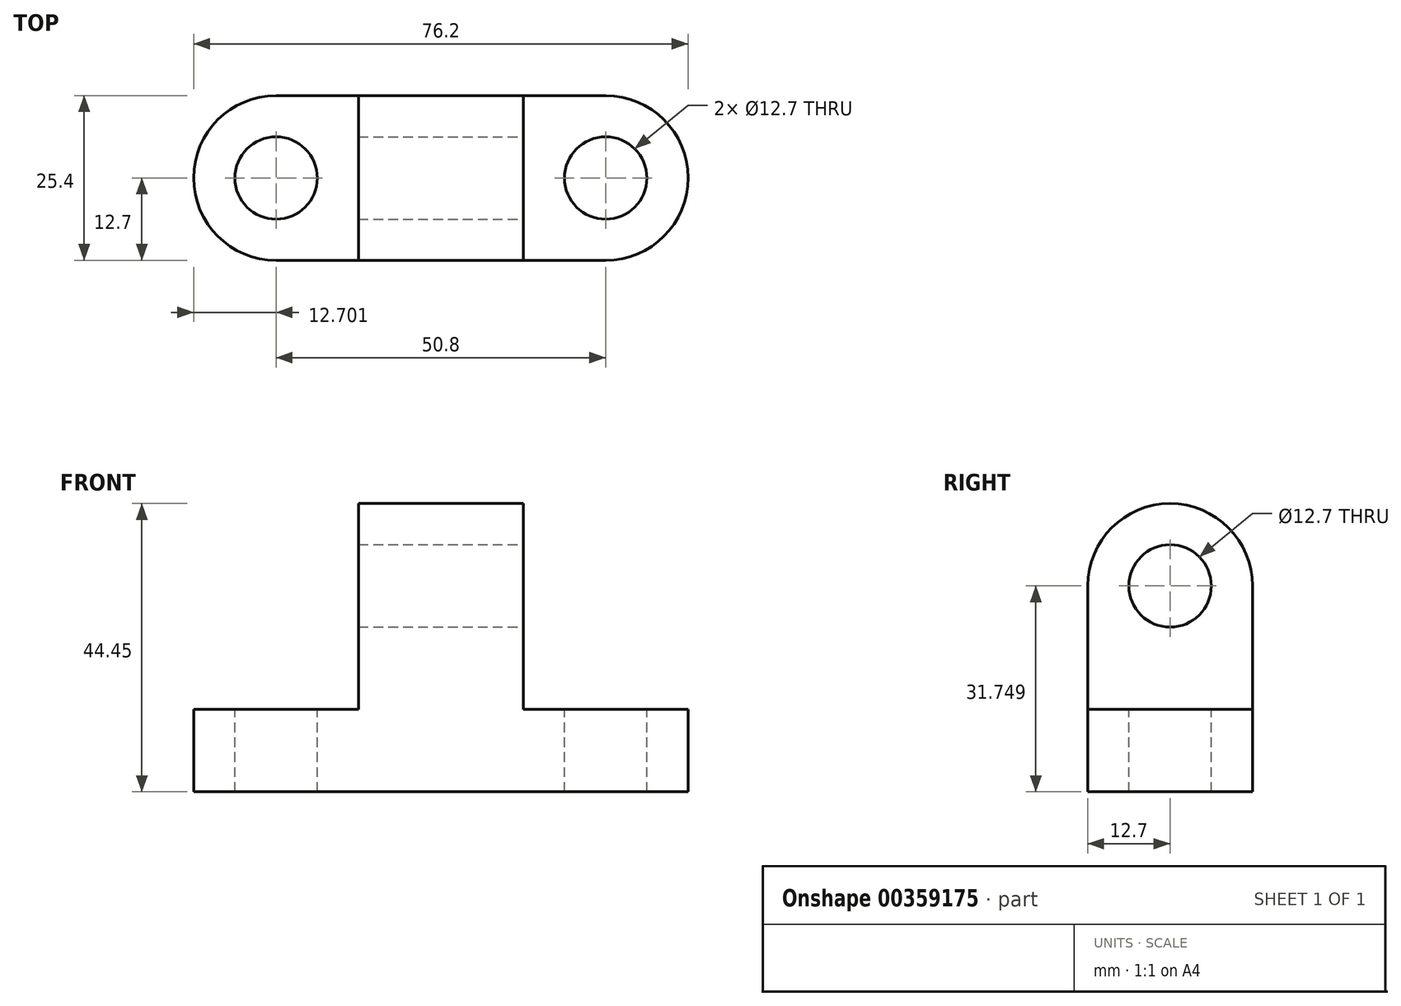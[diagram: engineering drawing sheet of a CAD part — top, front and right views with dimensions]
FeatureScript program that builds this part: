
annotation { "Feature Type Name" : "Feature", "Feature Type Description" : "" }
export const myFeature = defineFeature(function(context is Context, id is Id, definition is map)
    precondition{}
    {
        {
            var Q0;
            Q0=qCreatedBy(makeId("Front.planeOp"),FACE);
            var sketch = newSketch(context, id + "F0", { "sketchPlane" : qUnion([Q0])});
            skLineSegment(sketch, "E0", {"start": v(-54.44, 55.85) * mm, "end": v(-54.44, 24.1) * mm});
            skLineSegment(sketch, "E1", {"start": v(-54.44, 24.1) * mm, "end": v(-79.84, 24.1) * mm});
            skLineSegment(sketch, "E2", {"start": v(-79.84, 24.1) * mm, "end": v(-79.84, 11.4) * mm});
            skLineSegment(sketch, "E3", {"start": v(-79.84, 11.4) * mm, "end": v(-3.64, 11.4) * mm});
            skLineSegment(sketch, "E4", {"start": v(-3.64, 11.4) * mm, "end": v(-3.64, 24.1) * mm});
            skLineSegment(sketch, "E5", {"start": v(-3.64, 24.1) * mm, "end": v(-29.04, 24.1) * mm});
            skLineSegment(sketch, "E6", {"start": v(-29.04, 24.1) * mm, "end": v(-29.04, 55.85) * mm});
            skLineSegment(sketch, "E7", {"start": v(-29.04, 55.85) * mm, "end": v(-54.44, 55.85) * mm});
            skSolve(sketch);
        }
        {
            var Q0;
            Q0=makeQuery(id+"F0.imprint","IMPRINT",FACE,{"disambiguationData":[TD([[makeQuery(id+"F0.imprint","IMPRINT",EDGE,{"derivedFrom":sQuery(id+"F0.wireOp",EDGE,"E0")}),1.0]])]});
            extrude(context, id + "F1", {"entities" : qUnion([Q0]), "depth" : 25.4 * mm});
        }
        {
            var Q0;
            Q0=makeQuery(id+"F1.opExtrude","SWEPT_FACE",FACE,{"disambiguationData":[OSD([sQuery(id+"F0.wireOp",EDGE,"E6")])]});
            var sketch = newSketch(context, id + "F2", { "sketchPlane" : qUnion([Q0])});
            skLineSegment(sketch, "E8", {"start": v(-25.4, 24.1) * mm, "end": v(-25.4, 43.15) * mm});
            skLineSegment(sketch, "E9", {"start": v(-12.7, 55.85) * mm, "end": v(-12.7, 55.85) * mm});
            skLineSegment(sketch, "E10", {"start": v(0, 43.15) * mm, "end": v(0, 24.1) * mm});
            skPoint(sketch, "E11.visualSharp", {"position": v(-25.4, 55.85) * mm});
            skArc(sketch, "E11.filletArc", {"start": v(-12.7, 55.85) * mm, "mid": v(-21.68, 52.13) * mm, "end": v(-25.4, 43.15) * mm});
            skPoint(sketch, "E12.visualSharp", {"position": v(0, 55.85) * mm});
            skArc(sketch, "E12.filletArc", {"start": v(0, 43.15) * mm, "mid": v(-3.72, 52.13) * mm, "end": v(-12.7, 55.85) * mm});
            skCircle(sketch, "E13", {"center": v(-12.7, 43.15) * mm, "radius": 6.35 * mm});
            skSolve(sketch);
        }
        {
            var Q0;
            Q0=makeQuery(id+"F2.imprint","IMPRINT",FACE,{"disambiguationData":[TD([[makeQuery(id+"F2.imprint","IMPRINT",EDGE,{"derivedFrom":sQuery(id+"F2.wireOp",EDGE,"E13")}),1.0]])]});
            var Q1;
            {var subQ0=sQuery(id+"F2.wireOp",EDGE,"E11.filletArc");Q1=makeQuery(id+"F2.imprint","IMPRINT",FACE,{"disambiguationData":[TD([[makeQuery(id+"F2.imprint","IMPRINT",EDGE,{"derivedFrom":subQ0}),-1.0]])]});}
            var Q2;
            {var subQ0=sQuery(id+"F2.wireOp",EDGE,"E12.filletArc");Q2=makeQuery(id+"F2.imprint","IMPRINT",FACE,{"disambiguationData":[TD([[makeQuery(id+"F2.imprint","IMPRINT",EDGE,{"derivedFrom":subQ0}),-1.0]])]});}
            extrude(context, id + "F3", {"entities" : qUnion([Q0, Q1, Q2]), "operationType" : NewBodyOperationType.REMOVE, "oppositeDirection" : true, "depth" : 25.4 * mm});
        }
        {
            var Q0;
            Q0=makeQuery(id+"F1.opExtrude","SWEPT_FACE",FACE,{"disambiguationData":[OSD([sQuery(id+"F0.wireOp",EDGE,"E5")])]});
            var sketch = newSketch(context, id + "F4", { "sketchPlane" : qUnion([Q0])});
            skLineSegment(sketch, "E14", {"start": v(-29.04, 0) * mm, "end": v(-16.34, 0) * mm});
            skLineSegment(sketch, "E15", {"start": v(-3.64, -12.7) * mm, "end": v(-3.64, -12.7) * mm});
            skLineSegment(sketch, "E16", {"start": v(-16.34, -25.4) * mm, "end": v(-29.04, -25.4) * mm});
            skPoint(sketch, "E17.visualSharp", {"position": v(-3.64, 0) * mm});
            skArc(sketch, "E17.filletArc", {"start": v(-3.64, -12.7) * mm, "mid": v(-7.36, -3.72) * mm, "end": v(-16.34, 0) * mm});
            skPoint(sketch, "E18.visualSharp", {"position": v(-3.64, -25.4) * mm});
            skArc(sketch, "E18.filletArc", {"start": v(-16.34, -25.4) * mm, "mid": v(-7.36, -21.68) * mm, "end": v(-3.64, -12.7) * mm});
            skCircle(sketch, "E19", {"center": v(-16.34, -12.7) * mm, "radius": 6.35 * mm});
            skSolve(sketch);
        }
        {
            var Q0;
            Q0=makeQuery(id+"F1.opExtrude","SWEPT_FACE",FACE,{"disambiguationData":[OSD([sQuery(id+"F0.wireOp",EDGE,"E1")])]});
            var sketch = newSketch(context, id + "F5", { "sketchPlane" : qUnion([Q0])});
            skLineSegment(sketch, "E20", {"start": v(-54.44, 0) * mm, "end": v(-67.14, 0) * mm});
            skLineSegment(sketch, "E21", {"start": v(-79.84, -12.7) * mm, "end": v(-79.84, -12.7) * mm});
            skLineSegment(sketch, "E22", {"start": v(-67.14, -25.4) * mm, "end": v(-54.44, -25.4) * mm});
            skPoint(sketch, "E23.visualSharp", {"position": v(-79.84, 0) * mm});
            skArc(sketch, "E23.filletArc", {"start": v(-67.14, 0) * mm, "mid": v(-76.12, -3.72) * mm, "end": v(-79.84, -12.7) * mm});
            skPoint(sketch, "E24.visualSharp", {"position": v(-79.84, -25.4) * mm});
            skArc(sketch, "E24.filletArc", {"start": v(-79.84, -12.7) * mm, "mid": v(-76.12, -21.68) * mm, "end": v(-67.14, -25.4) * mm});
            skCircle(sketch, "E25", {"center": v(-67.14, -12.7) * mm, "radius": 6.35 * mm});
            skSolve(sketch);
        }
        {
            var Q0;
            Q0=makeQuery(id+"F4.imprint","IMPRINT",FACE,{"disambiguationData":[TD([[makeQuery(id+"F4.imprint","IMPRINT",EDGE,{"derivedFrom":sQuery(id+"F4.wireOp",EDGE,"E19")}),1.0]])]});
            var Q1;
            {var subQ0=sQuery(id+"F4.wireOp",EDGE,"E18.filletArc");Q1=makeQuery(id+"F4.imprint","IMPRINT",FACE,{"disambiguationData":[TD([[makeQuery(id+"F4.imprint","IMPRINT",EDGE,{"derivedFrom":subQ0}),-1.0]])]});}
            var Q2;
            {var subQ0=sQuery(id+"F5.wireOp",EDGE,"E24.filletArc");Q2=makeQuery(id+"F5.imprint","IMPRINT",FACE,{"disambiguationData":[TD([[makeQuery(id+"F5.imprint","IMPRINT",EDGE,{"derivedFrom":subQ0}),-1.0]])]});}
            var Q3;
            {var subQ0=sQuery(id+"F5.wireOp",EDGE,"E23.filletArc");Q3=makeQuery(id+"F5.imprint","IMPRINT",FACE,{"disambiguationData":[TD([[makeQuery(id+"F5.imprint","IMPRINT",EDGE,{"derivedFrom":subQ0}),-1.0]])]});}
            var Q4;
            Q4=makeQuery(id+"F5.imprint","IMPRINT",FACE,{"disambiguationData":[TD([[makeQuery(id+"F5.imprint","IMPRINT",EDGE,{"derivedFrom":sQuery(id+"F5.wireOp",EDGE,"E25")}),1.0]])]});
            var Q5;
            {var subQ0=sQuery(id+"F4.wireOp",EDGE,"E17.filletArc");Q5=makeQuery(id+"F4.imprint","IMPRINT",FACE,{"disambiguationData":[TD([[makeQuery(id+"F4.imprint","IMPRINT",EDGE,{"derivedFrom":subQ0}),-1.0]])]});}
            extrude(context, id + "F6", {"entities" : qUnion([Q0, Q1, Q2, Q3, Q4, Q5]), "operationType" : NewBodyOperationType.REMOVE, "oppositeDirection" : true, "depth" : 12.7 * mm});
        }
    });
